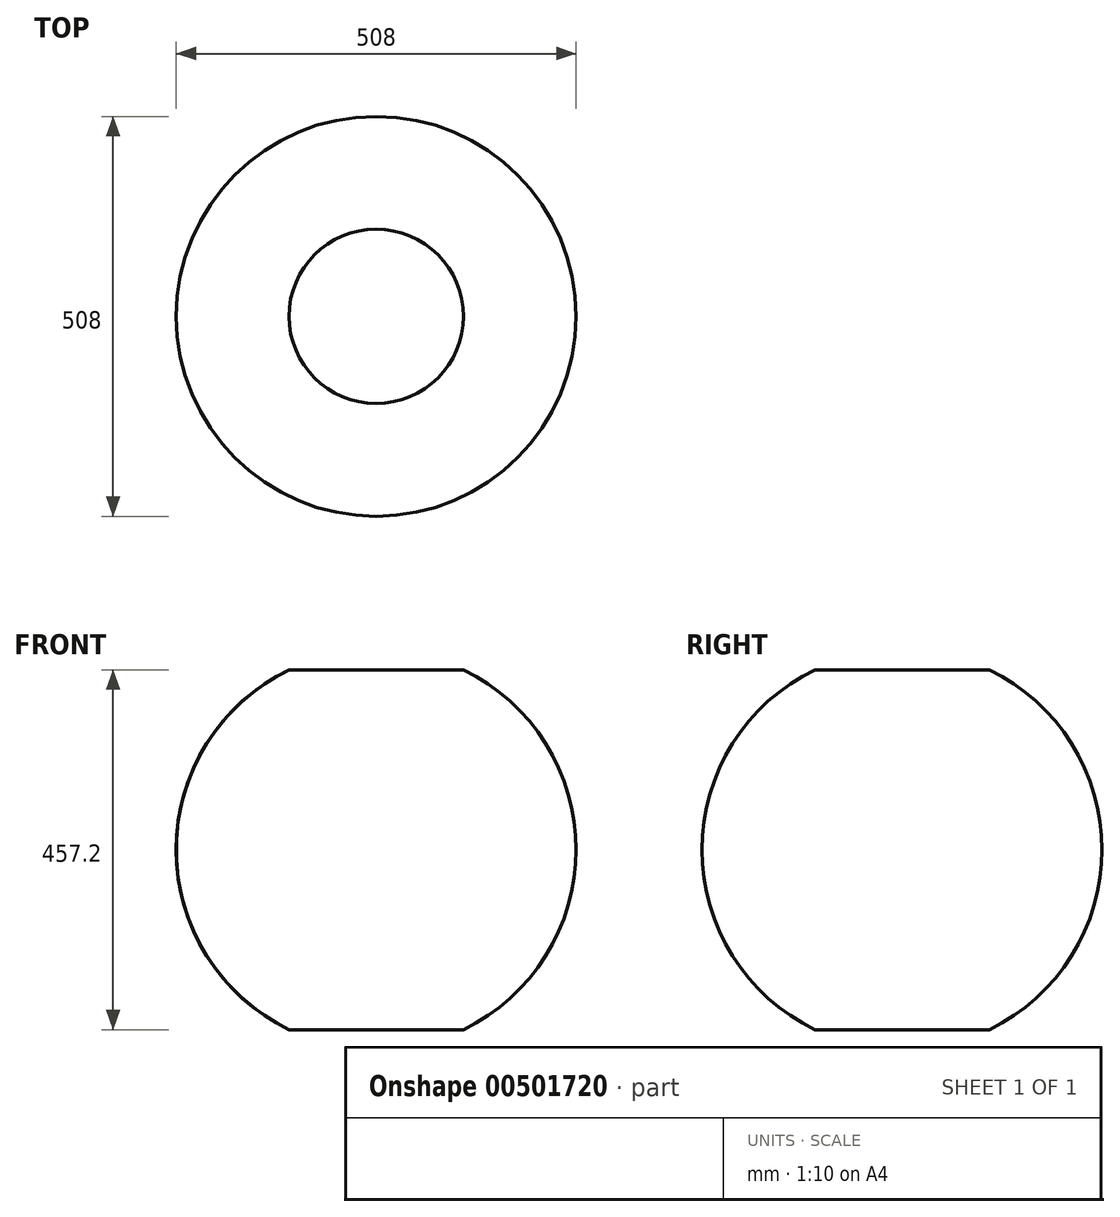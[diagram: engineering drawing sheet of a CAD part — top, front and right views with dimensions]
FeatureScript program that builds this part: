
annotation { "Feature Type Name" : "Feature", "Feature Type Description" : "" }
export const myFeature = defineFeature(function(context is Context, id is Id, definition is map)
    precondition{}
    {
        {
            var Q0;
            Q0=qCreatedBy(makeId("Front.planeOp"),FACE);
            var sketch = newSketch(context, id + "F0", { "sketchPlane" : qUnion([Q0])});
            skLineSegment(sketch, "E0", {"start": v(453.55, -378.26) * mm, "end": v(453.55, 78.94) * mm});
            skArc(sketch, "E1", {"start": v(564.26, -378.26) * mm, "mid": v(707.55, -149.66) * mm, "end": v(564.26, 78.94) * mm});
            skLineSegment(sketch, "E2.0", {"start": v(453.55, -378.26) * mm, "end": v(564.26, -378.26) * mm});
            skLineSegment(sketch, "E3.0", {"start": v(453.55, 78.94) * mm, "end": v(564.26, 78.94) * mm});
            skPoint(sketch, "E4.orphan", {"position": v(453.55, -403.66) * mm});
            skPoint(sketch, "E5.orphan", {"position": v(453.55, 104.34) * mm});
            skSolve(sketch);
        }
        {
            var Q0;
            Q0 = qSketchRegion(id + "F0", true);
            var Q1;
            Q1=sQuery(id+"F0.wireOp",EDGE,"E0");
            revolve(context, id + "F1", {"entities" : qUnion([Q0]), "axis" : qUnion([Q1]), "revolveType" : RevolveType.FULL});
        }
        {
            var Q0;
            Q0=qCreatedBy(makeId("Front.planeOp"),FACE);
            var sketch = newSketch(context, id + "F2", { "sketchPlane" : qUnion([Q0])});
            skLineSegment(sketch, "E6", {"start": v(7.85, -6.7) * mm, "end": v(30.56, -6.7) * mm});
            skLineSegment(sketch, "E7", {"start": v(6.33, -4.27) * mm, "end": v(31.43, -4.27) * mm});
            skLineSegment(sketch, "E8", {"start": v(31.43, 0) * mm, "end": v(5.36, 0) * mm});
            skLineSegment(sketch, "E9", {"start": v(5.36, 0) * mm, "end": v(5.36, 77.42) * mm});
            skLineSegment(sketch, "E10", {"start": v(5.36, 77.42) * mm, "end": v(29.05, 77.42) * mm});
            skLineSegment(sketch, "E11", {"start": v(29.05, 77.42) * mm, "end": v(31.43, 0) * mm});
            skLineSegment(sketch, "E12", {"start": v(30.56, -6.7) * mm, "end": v(31.43, -4.27) * mm});
            skLineSegment(sketch, "E13", {"start": v(6.33, -4.27) * mm, "end": v(7.85, -6.7) * mm});
            skSolve(sketch);
        }
        {
            var Q0;
            Q0=makeQuery(id+"F2.imprint","IMPRINT",FACE,{"disambiguationData":[TD([[makeQuery(id+"F2.imprint","IMPRINT",EDGE,{"derivedFrom":sQuery(id+"F2.wireOp",EDGE,"E8")}),-1.0]])]});
            var Q1;
            Q1=makeQuery(id+"F2.imprint","IMPRINT",FACE,{"disambiguationData":[TD([[makeQuery(id+"F2.imprint","IMPRINT",EDGE,{"derivedFrom":sQuery(id+"F2.wireOp",EDGE,"E6")}),1.0]])]});
            extrude(context, id + "F3", {"entities" : qUnion([Q0, Q1]), "operationType" : NewBodyOperationType.REMOVE, "endBound" : BoundingType.THROUGH_ALL, "oppositeDirection" : true, "depth" : 25.4 * mm});
        }
    });
